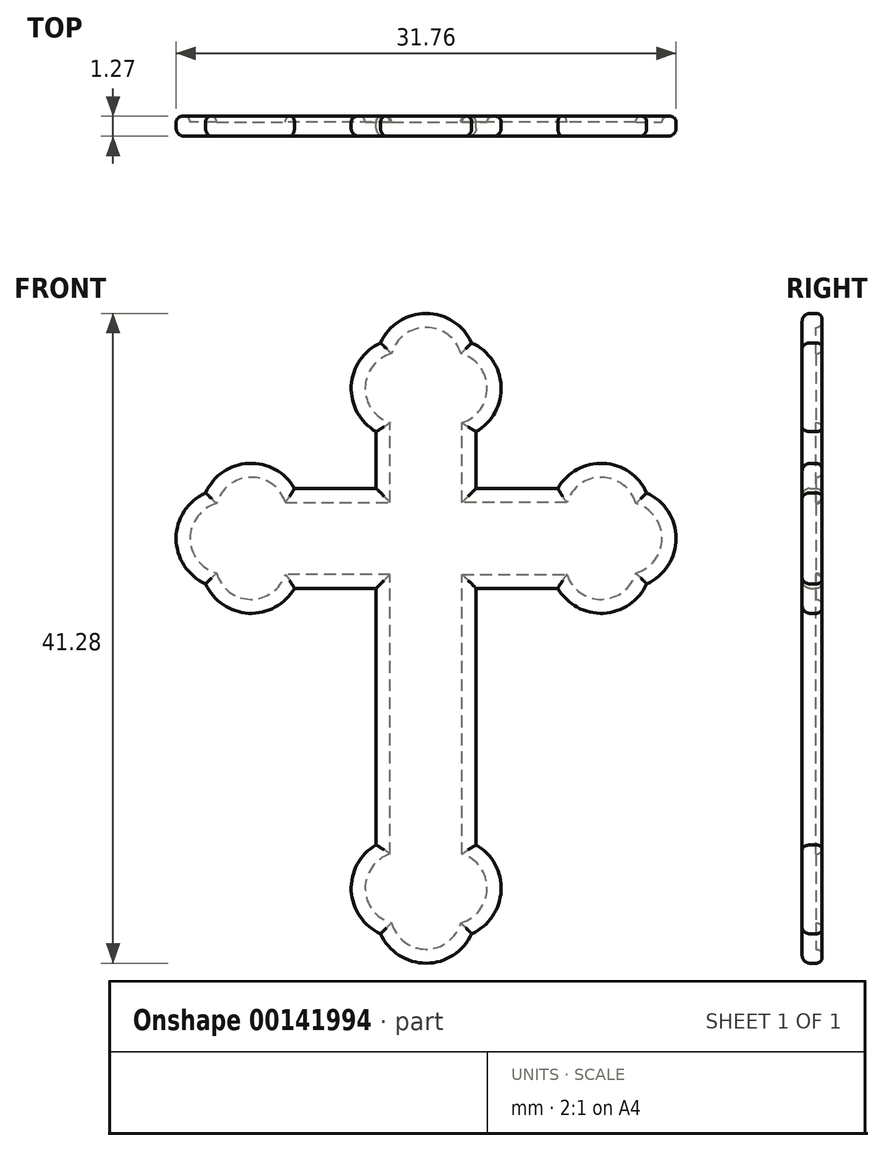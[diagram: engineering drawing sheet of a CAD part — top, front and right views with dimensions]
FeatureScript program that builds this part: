
annotation { "Feature Type Name" : "Feature", "Feature Type Description" : "" }
export const myFeature = defineFeature(function(context is Context, id is Id, definition is map)
    precondition{}
    {
        {
            var Q0;
            Q0=qCreatedBy(makeId("Front.planeOp"),FACE);
            var sketch = newSketch(context, id + "F0", { "sketchPlane" : qUnion([Q0])});
            skLineSegment(sketch, "E0", {"start": v(-3.17, 3.18) * mm, "end": v(-3.17, 6.78) * mm});
            skLineSegment(sketch, "E1", {"start": v(-3.17, 11.11) * mm, "end": v(0, 11.11) * mm, "construction": true});
            skLineSegment(sketch, "E2", {"start": v(0, 11.11) * mm, "end": v(0, -23.81) * mm, "construction": true});
            skLineSegment(sketch, "E3", {"start": v(0, -23.81) * mm, "end": v(-3.17, -23.81) * mm, "construction": true});
            skLineSegment(sketch, "E4", {"start": v(-3.17, -19.48) * mm, "end": v(-3.17, -3.17) * mm});
            skLineSegment(sketch, "E5", {"start": v(-3.17, -3.17) * mm, "end": v(-8.36, -3.17) * mm});
            skLineSegment(sketch, "E6", {"start": v(-12.7, -3.18) * mm, "end": v(-12.7, 0) * mm, "construction": true});
            skLineSegment(sketch, "E7", {"start": v(-8.36, 3.18) * mm, "end": v(-3.17, 3.18) * mm});
            skLineSegment(sketch, "E8", {"start": v(0, 0) * mm, "end": v(-12.7, 0) * mm, "construction": true});
            skLineSegment(sketch, "E9.MirrorCS", {"start": v(3.17, 3.18) * mm, "end": v(3.17, 6.78) * mm});
            skLineSegment(sketch, "E10.MirrorCS", {"start": v(3.17, -19.48) * mm, "end": v(3.17, -3.17) * mm});
            skLineSegment(sketch, "E11.MirrorCS", {"start": v(0, 0) * mm, "end": v(12.7, 0) * mm, "construction": true});
            skLineSegment(sketch, "E12.MirrorCS", {"start": v(12.7, -3.18) * mm, "end": v(12.7, 0) * mm, "construction": true});
            skLineSegment(sketch, "E13.MirrorCS", {"start": v(8.36, 3.18) * mm, "end": v(3.17, 3.18) * mm});
            skLineSegment(sketch, "E14.MirrorCS", {"start": v(3.17, -3.17) * mm, "end": v(8.36, -3.17) * mm});
            skArc(sketch, "E15", {"start": v(2.9, 12.42) * mm, "mid": v(0, 14.29) * mm, "end": v(-2.9, 12.42) * mm});
            skArc(sketch, "E16", {"start": v(-2.9, 12.42) * mm, "mid": v(-4.76, 9.68) * mm, "end": v(-3.17, 6.78) * mm});
            skLineSegment(sketch, "E17", {"start": v(-3.17, 11.11) * mm, "end": v(-1.59, 9.53) * mm, "construction": true});
            skLineSegment(sketch, "E18", {"start": v(0, 11.11) * mm, "end": v(-1.59, 9.53) * mm, "construction": true});
            skArc(sketch, "E19.MirrorCS", {"start": v(2.9, 12.42) * mm, "mid": v(4.76, 9.68) * mm, "end": v(3.17, 6.78) * mm});
            skPoint(sketch, "E20.orphan", {"position": v(3.17, 11.11) * mm});
            skArc(sketch, "E21", {"start": v(-14, 2.9) * mm, "mid": v(-15.88, 0) * mm, "end": v(-14, -2.9) * mm});
            skLineSegment(sketch, "E22", {"start": v(-12.7, -3.18) * mm, "end": v(-11.11, -1.59) * mm, "construction": true});
            skLineSegment(sketch, "E23", {"start": v(-11.11, -1.59) * mm, "end": v(-12.7, 0) * mm, "construction": true});
            skArc(sketch, "E24", {"start": v(-14, -2.9) * mm, "mid": v(-11.27, -4.76) * mm, "end": v(-8.36, -3.17) * mm});
            skArc(sketch, "E25.MirrorCS", {"start": v(-14, 2.9) * mm, "mid": v(-11.27, 4.76) * mm, "end": v(-8.36, 3.17) * mm});
            skPoint(sketch, "E26.orphan", {"position": v(-12.7, 3.17) * mm});
            skArc(sketch, "E27.MirrorCS", {"start": v(14, 2.9) * mm, "mid": v(11.27, 4.76) * mm, "end": v(8.36, 3.17) * mm});
            skArc(sketch, "E28.MirrorCS", {"start": v(14, 2.9) * mm, "mid": v(15.88, 0) * mm, "end": v(14, -2.9) * mm});
            skArc(sketch, "E29.MirrorCS", {"start": v(14, -2.9) * mm, "mid": v(11.27, -4.76) * mm, "end": v(8.36, -3.17) * mm});
            skPoint(sketch, "E30.orphan", {"position": v(12.7, 3.18) * mm});
            skArc(sketch, "E31", {"start": v(-2.9, -25.12) * mm, "mid": v(0, -26.99) * mm, "end": v(2.9, -25.12) * mm});
            skLineSegment(sketch, "E32", {"start": v(-3.17, -23.81) * mm, "end": v(-1.59, -22.23) * mm, "construction": true});
            skLineSegment(sketch, "E33", {"start": v(-1.59, -22.23) * mm, "end": v(0, -23.81) * mm, "construction": true});
            skArc(sketch, "E34", {"start": v(-3.17, -19.48) * mm, "mid": v(-4.76, -22.38) * mm, "end": v(-2.9, -25.12) * mm});
            skArc(sketch, "E35.MirrorCS", {"start": v(3.17, -19.48) * mm, "mid": v(4.76, -22.38) * mm, "end": v(2.9, -25.12) * mm});
            skSolve(sketch);
        }
        {
            var Q0;
            Q0=makeQuery(id+"F0.imprint","IMPRINT",FACE,{"disambiguationData":[TD([[makeQuery(id+"F0.imprint","IMPRINT",EDGE,{"derivedFrom":sQuery(id+"F0.wireOp",EDGE,"E0")}),-1.0]])]});
            extrude(context, id + "F1", {"entities" : qUnion([Q0]), "depth" : 1.27 * mm});
        }
        {
            var Q0;
            Q0=makeQuery(id+"F1.opExtrude","CAP_FACE",FACE,{"disambiguationData":[OSD([sQuery(id+"F0.wireOp",EDGE,"E0"),sQuery(id+"F0.wireOp",EDGE,"E4"),sQuery(id+"F0.wireOp",EDGE,"E5"),sQuery(id+"F0.wireOp",EDGE,"E7"),sQuery(id+"F0.wireOp",EDGE,"E9.MirrorCS"),sQuery(id+"F0.wireOp",EDGE,"E10.MirrorCS"),sQuery(id+"F0.wireOp",EDGE,"E13.MirrorCS"),sQuery(id+"F0.wireOp",EDGE,"E14.MirrorCS"),sQuery(id+"F0.wireOp",EDGE,"E15"),sQuery(id+"F0.wireOp",EDGE,"E16"),sQuery(id+"F0.wireOp",EDGE,"E19.MirrorCS"),sQuery(id+"F0.wireOp",EDGE,"E21"),sQuery(id+"F0.wireOp",EDGE,"E24"),sQuery(id+"F0.wireOp",EDGE,"E25.MirrorCS"),sQuery(id+"F0.wireOp",EDGE,"E27.MirrorCS"),sQuery(id+"F0.wireOp",EDGE,"E28.MirrorCS"),sQuery(id+"F0.wireOp",EDGE,"E29.MirrorCS"),sQuery(id+"F0.wireOp",EDGE,"E31"),sQuery(id+"F0.wireOp",EDGE,"E34"),sQuery(id+"F0.wireOp",EDGE,"E35.MirrorCS")])],"isStart":false});
            fillet(context, id + "F2", {"entities" : qUnion([Q0]), "radius" : 0.5 * mm, "tangentPropagation" : true, "allowEdgeOverflow" : false});
        }
        {
            var Q0;
            Q0=makeQuery(id+"F1.opExtrude","CAP_FACE",FACE,{"disambiguationData":[OSD([sQuery(id+"F0.wireOp",EDGE,"E0"),sQuery(id+"F0.wireOp",EDGE,"E4"),sQuery(id+"F0.wireOp",EDGE,"E5"),sQuery(id+"F0.wireOp",EDGE,"E7"),sQuery(id+"F0.wireOp",EDGE,"E9.MirrorCS"),sQuery(id+"F0.wireOp",EDGE,"E10.MirrorCS"),sQuery(id+"F0.wireOp",EDGE,"E13.MirrorCS"),sQuery(id+"F0.wireOp",EDGE,"E14.MirrorCS"),sQuery(id+"F0.wireOp",EDGE,"E15"),sQuery(id+"F0.wireOp",EDGE,"E16"),sQuery(id+"F0.wireOp",EDGE,"E19.MirrorCS"),sQuery(id+"F0.wireOp",EDGE,"E21"),sQuery(id+"F0.wireOp",EDGE,"E24"),sQuery(id+"F0.wireOp",EDGE,"E25.MirrorCS"),sQuery(id+"F0.wireOp",EDGE,"E27.MirrorCS"),sQuery(id+"F0.wireOp",EDGE,"E28.MirrorCS"),sQuery(id+"F0.wireOp",EDGE,"E29.MirrorCS"),sQuery(id+"F0.wireOp",EDGE,"E31"),sQuery(id+"F0.wireOp",EDGE,"E34"),sQuery(id+"F0.wireOp",EDGE,"E35.MirrorCS")])],"isStart":true});
            shell(context, id + "F3", {"entities" : qUnion([Q0]), "thickness" : 0.89 * mm});
        }
        {
            var Q0;
            Q0=makeQuery(id+"F1.opExtrude","CAP_FACE",FACE,{"disambiguationData":[OSD([sQuery(id+"F0.wireOp",EDGE,"E0"),sQuery(id+"F0.wireOp",EDGE,"E4"),sQuery(id+"F0.wireOp",EDGE,"E5"),sQuery(id+"F0.wireOp",EDGE,"E7"),sQuery(id+"F0.wireOp",EDGE,"E9.MirrorCS"),sQuery(id+"F0.wireOp",EDGE,"E10.MirrorCS"),sQuery(id+"F0.wireOp",EDGE,"E13.MirrorCS"),sQuery(id+"F0.wireOp",EDGE,"E14.MirrorCS"),sQuery(id+"F0.wireOp",EDGE,"E15"),sQuery(id+"F0.wireOp",EDGE,"E16"),sQuery(id+"F0.wireOp",EDGE,"E19.MirrorCS"),sQuery(id+"F0.wireOp",EDGE,"E21"),sQuery(id+"F0.wireOp",EDGE,"E24"),sQuery(id+"F0.wireOp",EDGE,"E25.MirrorCS"),sQuery(id+"F0.wireOp",EDGE,"E27.MirrorCS"),sQuery(id+"F0.wireOp",EDGE,"E28.MirrorCS"),sQuery(id+"F0.wireOp",EDGE,"E29.MirrorCS"),sQuery(id+"F0.wireOp",EDGE,"E31"),sQuery(id+"F0.wireOp",EDGE,"E34"),sQuery(id+"F0.wireOp",EDGE,"E35.MirrorCS")])],"isStart":true});
            fillet(context, id + "F4", {"entities" : qUnion([Q0]), "radius" : 0.38 * mm, "tangentPropagation" : true, "allowEdgeOverflow" : false});
        }
    });
